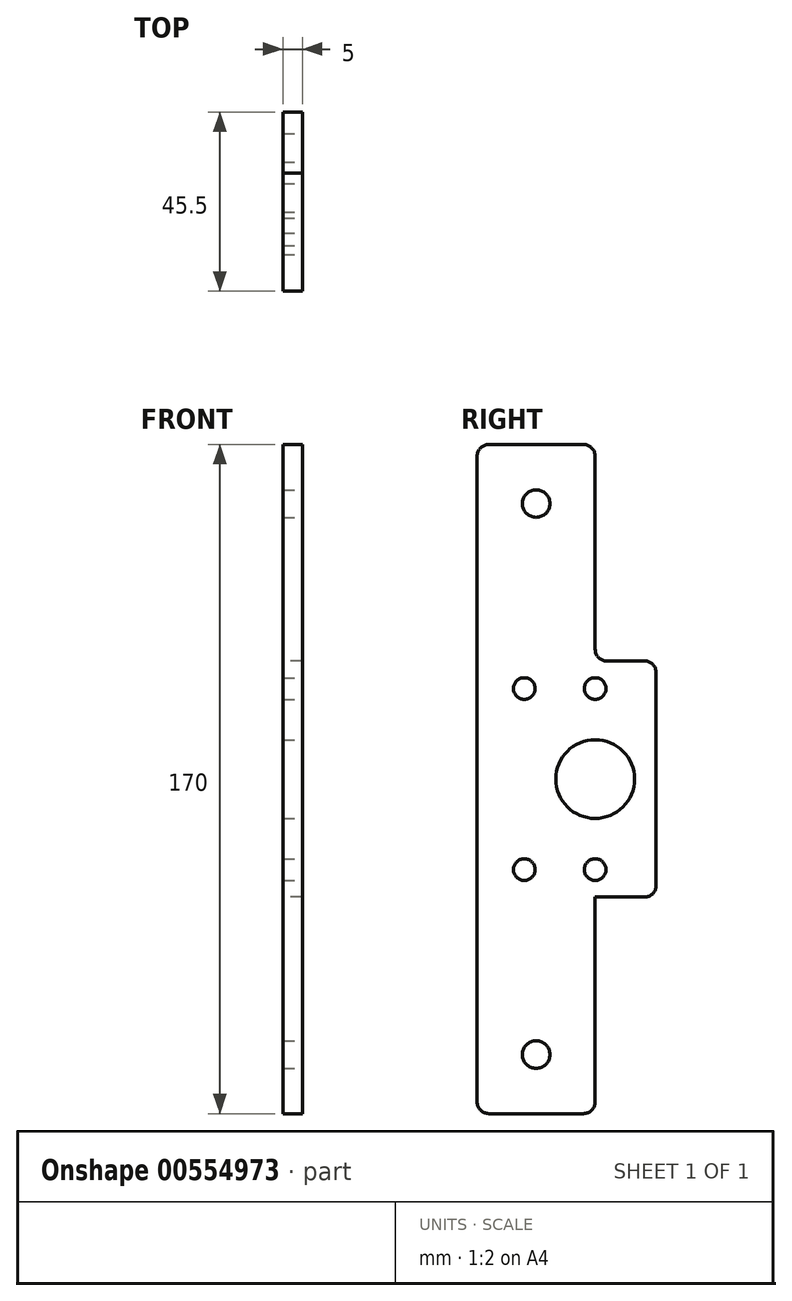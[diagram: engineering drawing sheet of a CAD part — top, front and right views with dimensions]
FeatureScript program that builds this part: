
annotation { "Feature Type Name" : "Feature", "Feature Type Description" : "" }
export const myFeature = defineFeature(function(context is Context, id is Id, definition is map)
    precondition{}
    {
        {
            var Q0;
            Q0=qCreatedBy(makeId("Right.planeOp"),FACE);
            var sketch = newSketch(context, id + "F0", { "sketchPlane" : qUnion([Q0])});
            skLineSegment(sketch, "E0.bottom", {"start": v(15, 85) * mm, "end": v(-15, 85) * mm});
            skLineSegment(sketch, "E0.top", {"start": v(15, -85) * mm, "end": v(-15, -85) * mm});
            skLineSegment(sketch, "E0.left", {"start": v(15, 85) * mm, "end": v(15, 30) * mm});
            skLineSegment(sketch, "E0.right", {"start": v(-15, 85) * mm, "end": v(-15, -85) * mm});
            skPoint(sketch, "E0.middle", {"position": v(0, 0) * mm});
            skLineSegment(sketch, "E1", {"start": v(15, 30) * mm, "end": v(30.5, 30) * mm});
            skLineSegment(sketch, "E2", {"start": v(30.5, 30) * mm, "end": v(30.5, -30) * mm});
            skLineSegment(sketch, "E3", {"start": v(30.5, -30) * mm, "end": v(15, -30) * mm});
            skLineSegment(sketch, "E4.trimOffspring", {"start": v(15, -30) * mm, "end": v(15, -85) * mm});
            skSolve(sketch);
        }
        {
            var Q0;
            Q0 = qSketchRegion(id + "F0", true);
            extrude(context, id + "F1", {"entities" : qUnion([Q0]), "depth" : 5 * mm, "offsetDistance" : 25 * mm});
        }
        {
            var Q0;
            Q0=makeQuery(id+"F1.opExtrude","SWEPT_EDGE",EDGE,{"disambiguationData":[OSD([sQuery(id+"F0.wireOp",EDGE,"E0.top"),sQuery(id+"F0.wireOp",EDGE,"E0.left")])]});
            var Q1;
            Q1=makeQuery(id+"F1.opExtrude","SWEPT_EDGE",EDGE,{"disambiguationData":[OSD([sQuery(id+"F0.wireOp",EDGE,"E0.bottom"),sQuery(id+"F0.wireOp",EDGE,"E0.right")])]});
            var Q2;
            Q2=makeQuery(id+"F1.opExtrude","SWEPT_EDGE",EDGE,{"disambiguationData":[OSD([sQuery(id+"F0.wireOp",EDGE,"E0.bottom"),sQuery(id+"F0.wireOp",EDGE,"E0.left")])]});
            var Q3;
            Q3=makeQuery(id+"F1.opExtrude","SWEPT_EDGE",EDGE,{"disambiguationData":[OSD([sQuery(id+"F0.wireOp",EDGE,"E0.top"),sQuery(id+"F0.wireOp",EDGE,"E0.right")])]});
            fillet(context, id + "F2", {"entities" : qUnion([Q0, Q1, Q2, Q3]), "radius" : 3 * mm, "tangentPropagation" : true, "allowEdgeOverflow" : false});
        }
        {
            var Q0;
            Q0=makeQuery(id+"F1.opExtrude","CAP_FACE",FACE,{"disambiguationData":[OSD([sQuery(id+"F0.wireOp",EDGE,"E0.bottom"),sQuery(id+"F0.wireOp",EDGE,"E0.top"),sQuery(id+"F0.wireOp",EDGE,"E0.left"),sQuery(id+"F0.wireOp",EDGE,"E0.right")])],"isStart":false});
            var sketch = newSketch(context, id + "F3", { "sketchPlane" : qUnion([Q0])});
            skCircle(sketch, "E5", {"center": v(0, 70) * mm, "radius": 3.5 * mm});
            skCircle(sketch, "E6.MirrorC", {"center": v(0, -70) * mm, "radius": 3.5 * mm});
            skPoint(sketch, "E7.center.orphan", {"position": v(0, 40) * mm});
            skSolve(sketch);
        }
        {
            var Q0;
            Q0 = qSketchRegion(id + "F3", true);
            extrude(context, id + "F4", {"entities" : qUnion([Q0]), "operationType" : NewBodyOperationType.REMOVE, "oppositeDirection" : true, "depth" : 5 * mm, "offsetDistance" : 25 * mm});
        }
        {
            var Q0;
            Q0=makeQuery(id+"F1.opExtrude","SWEPT_EDGE",EDGE,{"disambiguationData":[OSD([sQuery(id+"F0.wireOp",EDGE,"E1"),sQuery(id+"F0.wireOp",EDGE,"E2")])]});
            var Q1;
            Q1=makeQuery(id+"F1.opExtrude","SWEPT_EDGE",EDGE,{"disambiguationData":[OSD([sQuery(id+"F0.wireOp",EDGE,"E2"),sQuery(id+"F0.wireOp",EDGE,"E3")])]});
            fillet(context, id + "F5", {"entities" : qUnion([Q0, Q1]), "radius" : 3 * mm, "tangentPropagation" : true, "allowEdgeOverflow" : false});
        }
        {
            var Q0;
            Q0=makeQuery(id+"F1.opExtrude","CAP_FACE",FACE,{"disambiguationData":[OSD([sQuery(id+"F0.wireOp",EDGE,"E0.bottom"),sQuery(id+"F0.wireOp",EDGE,"E0.top"),sQuery(id+"F0.wireOp",EDGE,"E0.left"),sQuery(id+"F0.wireOp",EDGE,"E0.right"),sQuery(id+"F0.wireOp",EDGE,"E1"),sQuery(id+"F0.wireOp",EDGE,"E2"),sQuery(id+"F0.wireOp",EDGE,"E3"),sQuery(id+"F0.wireOp",EDGE,"E4.trimOffspring")])],"isStart":false});
            var sketch = newSketch(context, id + "F6", { "sketchPlane" : qUnion([Q0])});
            skCircle(sketch, "E8", {"center": v(15, 0) * mm, "radius": 10 * mm});
            skCircle(sketch, "E9", {"center": v(15, 23) * mm, "radius": 2.75 * mm});
            skCircle(sketch, "E10", {"center": v(15, -23) * mm, "radius": 2.75 * mm});
            skCircle(sketch, "E11", {"center": v(-3, -23) * mm, "radius": 2.75 * mm});
            skCircle(sketch, "E12", {"center": v(-3, 23) * mm, "radius": 2.75 * mm});
            skSolve(sketch);
        }
        {
            var Q0;
            Q0 = qSketchRegion(id + "F6", true);
            extrude(context, id + "F7", {"entities" : qUnion([Q0]), "operationType" : NewBodyOperationType.REMOVE, "oppositeDirection" : true, "depth" : 5 * mm, "offsetDistance" : 25 * mm});
        }
    });
